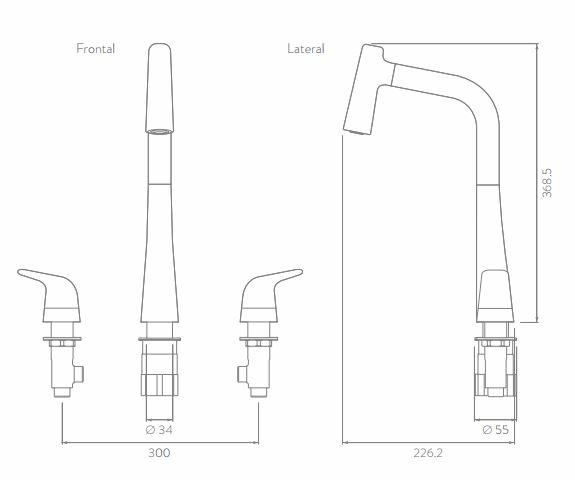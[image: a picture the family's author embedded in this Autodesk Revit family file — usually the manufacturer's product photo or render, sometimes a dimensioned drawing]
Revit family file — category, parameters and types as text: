
# Revit family: LQ5000001_Lavaplatos Monocontrol Liquid
name_source: partatom
category: Aparatos sanitarios
units: mm (PartAtom-declared; Revit-internal decimal feet)

## family parameters
Anfitrión = Cara
Compartido = No
Corte con vacíos al cargar = No
Cota de conector redondo = Diámetro de uso
Número OmniClass = 23.31.11.00
Punto de cálculo de habitación = No
Tipo de pieza = Normal
Título OmniClass = Faucets

## types (1)
- LQ5000001_Lavaplatos Monocontrol Liquid
    Alto = 368 mm  [stored 1.20735 ft]
    Ancho = 55 mm
    Capacidad de flujo estimada real a 60 psi = 5,6 L/min.
    Conexión AC = Sí
    Conexión AF = Sí
    Conexión de residuos = Sí
    Creado por = IDD
    Descripción = La línea de griferías, duchas y accesorios Liquid se inspira en la tensión superficial del agua
y en cómo esta crea formas armoniosas adaptándose al ambiente. Al igual que el agua,
las superficies de las griferías Liquid juegan con la luz y los reflejos que fluyen alrededor
de sus formas, sus líneas continuas y simplicidad formal proporcionan la ventaja práctica,
limpieza sin esfuerzo
    Diámetro desagüe = 15 mm  [stored 0.0492126 ft]
    Elevación por defecto = 1219 mm
    Fabricante = Corona
    Fabrication place = Colombia
    Fecha de creación = 14/08/2020
    Garantía = 30 años
    Material = Corona_Metálico
    Peso  Bruto = 2.600 g. - 5,73 lb.
    Peso neto = .350 g. - 5,18 lb.
    Presion maxima = 125 psi (860 Kpa).
    Presion minima = 20 psi (140 Kpa).
    Profundidad = 226 mm  [stored 0.74147 ft]
    Reference = LQ5010001
    Temperatura máxima de trabajo = 71°C / 159,8°F
    Temperatura mínima de Trabajo = 5°C / 41 °F
    URL = https://corona.co
    Vida útil o desgaste (unidad) = 500.000 ciclos.
    Warranty = 30 años
    Weight = 2500 g

note: [stored X ft] marks values corroborated as IEEE doubles in the binary element streams (Revit-internal decimal feet)

## geometry (parser evidence)
native form markers: Blend x3, Extrusion x1, Sweep x4
no freeform markers — native parametric forms only
